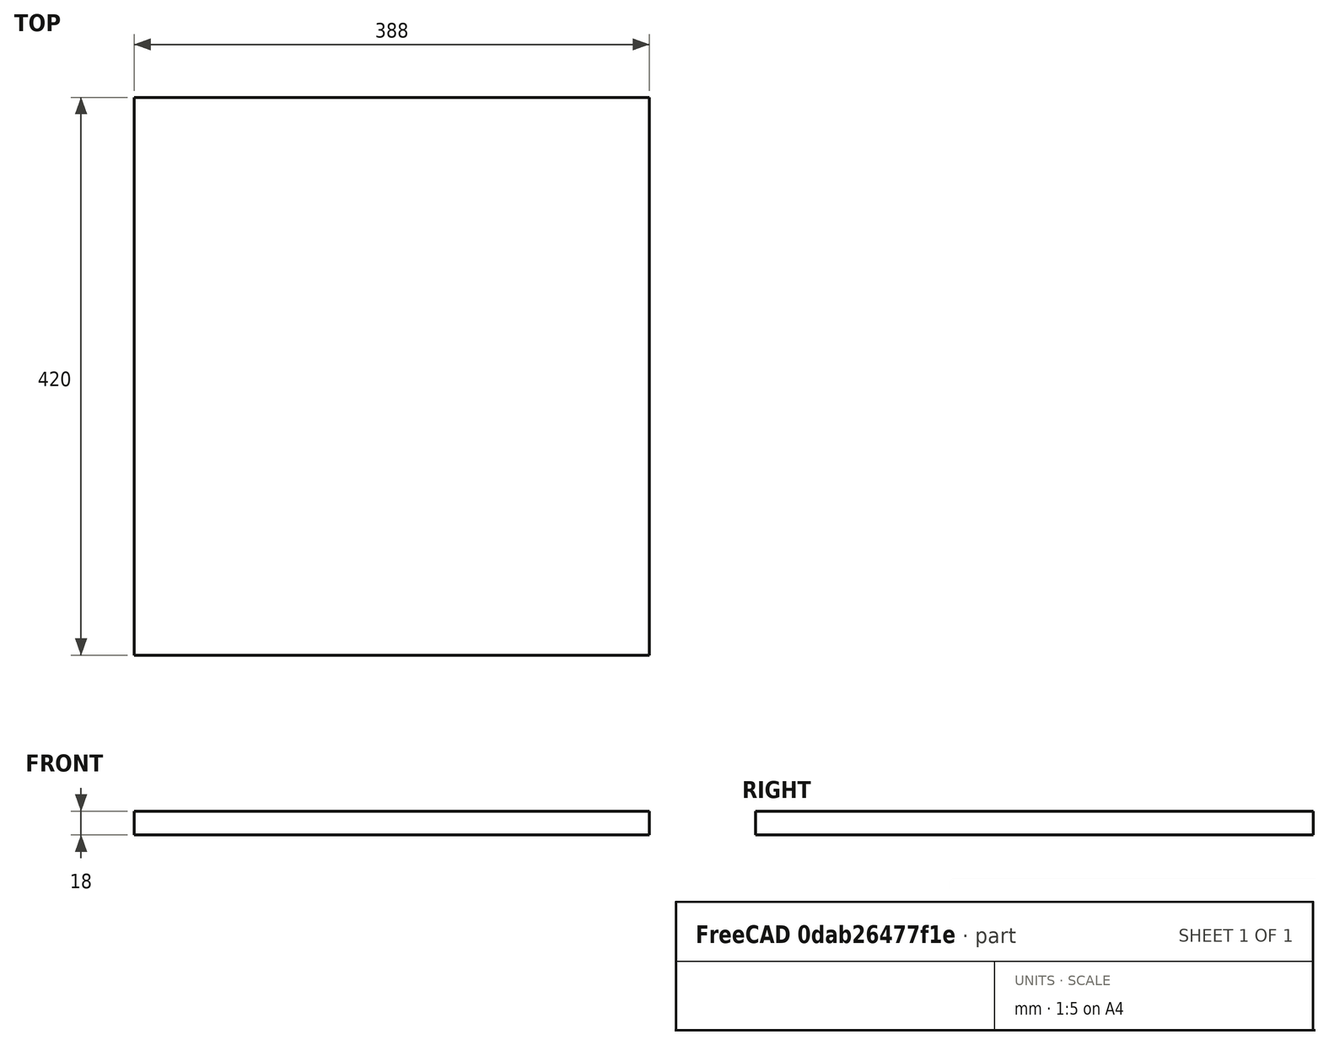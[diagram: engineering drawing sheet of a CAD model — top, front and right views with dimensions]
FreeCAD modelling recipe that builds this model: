
FCSTD DOCUMENT  (FreeCAD 0.18R4 (GitTag))
Label: bottom_shelf_1
License: All rights reserved
LicenseURL: http://en.wikipedia.org/wiki/All_rights_reserved
objects: Sketcher::SketchObject×1, PartDesign::Pad×1, PartDesign::Body×1
note: 4 computed .brp shape members not serialized (recipe doc carries the construction recipe); baked Part::Feature solids carry a one-line shape summary decoded from their .brp

FEATURE [Sketcher::SketchObject] Sketch
  MapMode = 5
  Support = -> [XY_Plane]
  sketch-geometry (4):
    g0: LineSegment StartX=0 StartY=0 StartZ=0 EndX=-388 EndY=0 EndZ=0
    g1: LineSegment StartX=-388 StartY=0 StartZ=0 EndX=-388 EndY=420 EndZ=0
    g2: LineSegment StartX=-388 StartY=420 StartZ=0 EndX=0 EndY=420 EndZ=0
    g3: LineSegment StartX=0 StartY=420 StartZ=0 EndX=0 EndY=0 EndZ=0
  constraints (11):
    c: Coincident(g0,g1)
    c: Coincident(g1,g2)
    c: Coincident(g2,g3)
    c: Coincident(g3,g0)
    c: Horizontal(g0)
    c: Horizontal(g2)
    c: Vertical(g1)
    c: Vertical(g3)
    c: Coincident(g0,g-1)
    c: DistanceY(g3,g3) = 420
    c: DistanceX(g0,g0) = 388
FEATURE [PartDesign::Pad] Pad
  Length = 18
  Length2 = 100
  Profile = -> Sketch
  Type = 0
FEATURE [PartDesign::Body] Body
  Group = -> [Sketch,Pad]
  Origin = -> Origin
  Tip = -> Pad
